# Revit family: VTp758 Угольник с накидной гайкой
name_source: partatom
category: Соединительные детали трубопроводов
revit_build: Autodesk Revit 2015 (Build: 20140606_1530(x64)
units: mm (PartAtom-declared; Revit-internal decimal feet)

## types (4) — shared parameters
Группа модели = VTp.700
Изготовитель = VALTEC S.R.L.
Коэффициент K = 0.5
Метод определения потерь = Коэффициент K
Описание = Угольник с накидной гайкой
Таблица коэффициентов K = Angle Valve Threaded

## per-type parameters (varying)
| type | 20х1/2" | 20х3/4" | 25х1" | 25х3/4" | A | B | C | G | Lrez | d | Глубина вхождения | Код по классификатору |
| 20х1/2" | Да | Нет | Нет | Нет | 27 мм | 15 мм | 48 мм | 15 мм | 10 мм | 20 мм | 8 мм | VTp.758.0.02004 |
| 20х3/4" | Нет | Да | Нет | Нет | 27 мм | 15 мм | 50 мм | 20 мм | 10 мм | 20 мм | 8 мм | VTp.758.0.02005 |
| 25х1" | Нет | Нет | Да | Нет | 34 мм | 17 мм | 60 мм | 25 мм | 14 мм | 25 мм | 11 мм | VTp.758.0.02506 |
| 25х3/4" | Нет | Нет | Нет | Да | 31 мм | 17 мм | 50 мм | 20 мм | 10 мм | 25 мм | 8 мм | VTp.758.0.02505 |
